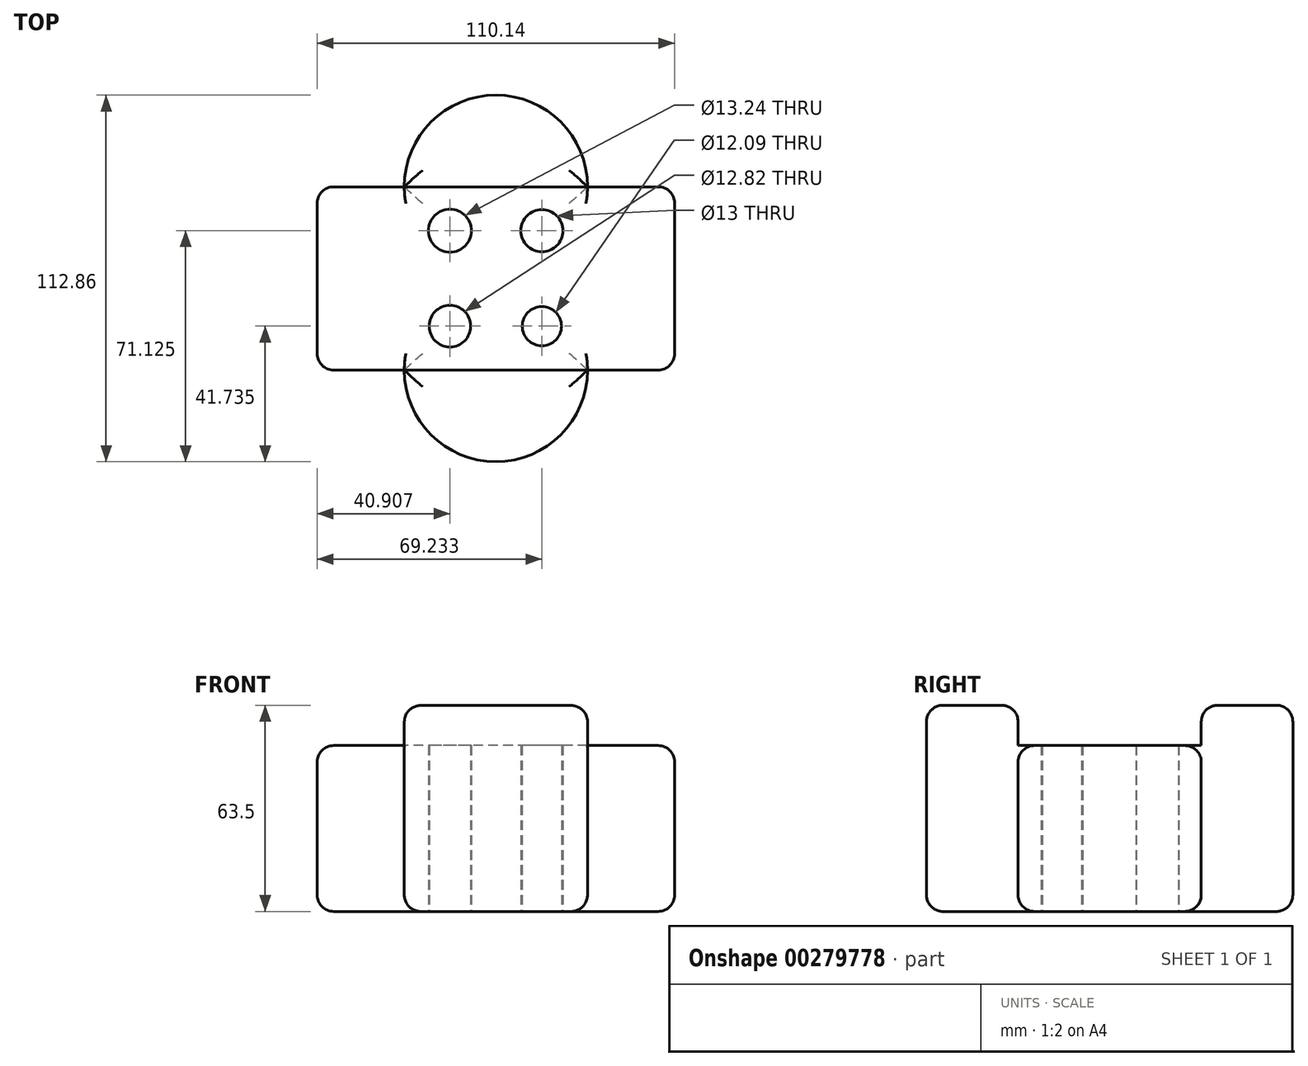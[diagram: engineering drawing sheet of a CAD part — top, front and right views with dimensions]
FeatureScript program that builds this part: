
annotation { "Feature Type Name" : "Feature", "Feature Type Description" : "" }
export const myFeature = defineFeature(function(context is Context, id is Id, definition is map)
    precondition{}
    {
        {
            var Q0;
            Q0=qCreatedBy(makeId("Top.planeOp"),FACE);
            var sketch = newSketch(context, id + "F0", { "sketchPlane" : qUnion([Q0])});
            skLineSegment(sketch, "E0.bottom", {"start": v(55.07, 28.22) * mm, "end": v(-55.07, 28.22) * mm});
            skLineSegment(sketch, "E0.top", {"start": v(55.07, -28.22) * mm, "end": v(-55.07, -28.22) * mm});
            skLineSegment(sketch, "E0.left", {"start": v(55.07, 28.22) * mm, "end": v(55.07, -28.22) * mm});
            skLineSegment(sketch, "E0.right", {"start": v(-55.07, 28.22) * mm, "end": v(-55.07, -28.22) * mm});
            skPoint(sketch, "E0.middle", {"position": v(0, 0) * mm});
            skCircle(sketch, "E1", {"center": v(0, 28.22) * mm, "radius": 28.22 * mm});
            skCircle(sketch, "E2", {"center": v(0, -28.22) * mm, "radius": 28.22 * mm});
            skLineSegment(sketch, "E3.bottom", {"start": v(14.16, 14.7) * mm, "end": v(-14.16, 14.7) * mm});
            skLineSegment(sketch, "E3.top", {"start": v(14.16, -14.7) * mm, "end": v(-14.16, -14.7) * mm});
            skLineSegment(sketch, "E3.left", {"start": v(14.16, 14.7) * mm, "end": v(14.16, -14.7) * mm});
            skLineSegment(sketch, "E3.right", {"start": v(-14.16, 14.7) * mm, "end": v(-14.16, -14.7) * mm});
            skCircle(sketch, "E4", {"center": v(14.16, 14.7) * mm, "radius": 6.5 * mm});
            skCircle(sketch, "E5", {"center": v(-14.16, 14.7) * mm, "radius": 6.62 * mm});
            skCircle(sketch, "E6", {"center": v(-14.16, -14.7) * mm, "radius": 6.4 * mm});
            skCircle(sketch, "E7", {"center": v(14.16, -14.7) * mm, "radius": 6.04 * mm});
            skSolve(sketch);
        }
        {
            var Q0;
            {var subQ5=sQuery(id+"F0.wireOp",EDGE,"E0.right");Q0=makeQuery(id+"F0.imprint","IMPRINT",FACE,{"disambiguationData":[TD([[makeQuery(id+"F0.imprint","IMPRINT",EDGE,{"derivedFrom":subQ5}),1.0]])]});}
            var Q1;
            {var subQ0=sQuery(id+"F0.wireOp",EDGE,"E2");var subQ1=sQuery(id+"F0.wireOp",EDGE,"E0.top");var subQ2=makeQuery(id+"F0.imprint","INTERSECT",VERTEX,{"disambiguationData":[OD(0.0)],"derivedFrom":[subQ1,subQ0]});Q1=makeQuery(id+"F0.imprint","IMPRINT",FACE,{"disambiguationData":[TD([[makeQuery(id+"F0.imprint","IMPRINT",EDGE,{"disambiguationData":[TD([[subQ2,-1.0]])],"derivedFrom":subQ1}),-1.0]])]});}
            var Q2;
            {var subQ0=sQuery(id+"F0.wireOp",EDGE,"E1");var subQ1=sQuery(id+"F0.wireOp",EDGE,"E0.bottom");var subQ2=makeQuery(id+"F0.imprint","INTERSECT",VERTEX,{"disambiguationData":[OD(0.0)],"derivedFrom":[subQ1,subQ0]});Q2=makeQuery(id+"F0.imprint","IMPRINT",FACE,{"disambiguationData":[TD([[makeQuery(id+"F0.imprint","IMPRINT",EDGE,{"disambiguationData":[TD([[subQ2,-1.0]])],"derivedFrom":subQ1}),1.0]])]});}
            var Q3;
            {var subQ0=sQuery(id+"F0.wireOp",EDGE,"E0.left");Q3=makeQuery(id+"F0.imprint","IMPRINT",FACE,{"disambiguationData":[TD([[makeQuery(id+"F0.imprint","IMPRINT",EDGE,{"derivedFrom":subQ0}),-1.0]])]});}
            var Q4;
            {var subQ0=sQuery(id+"F0.wireOp",EDGE,"E3.right");var subQ1=sQuery(id+"F0.wireOp",EDGE,"E1");var subQ2=makeQuery(id+"F0.imprint","INTERSECT",VERTEX,{"derivedFrom":[subQ1,subQ0]});Q4=makeQuery(id+"F0.imprint","IMPRINT",FACE,{"disambiguationData":[TD([[makeQuery(id+"F0.imprint","IMPRINT",EDGE,{"disambiguationData":[TD([[subQ2,-1.0]])],"derivedFrom":subQ1}),-1.0]])]});}
            var Q5;
            {var subQ0=sQuery(id+"F0.wireOp",EDGE,"E2");var subQ1=sQuery(id+"F0.wireOp",EDGE,"E1");var subQ2=makeQuery(id+"F0.imprint","INTERSECT",VERTEX,{"derivedFrom":[subQ1,subQ0]});Q5=makeQuery(id+"F0.imprint","IMPRINT",FACE,{"disambiguationData":[TD([[makeQuery(id+"F0.imprint","IMPRINT",EDGE,{"disambiguationData":[TD([[subQ2,-1.0]])],"derivedFrom":subQ1}),-1.0]])]});}
            var Q6;
            {var subQ5=sQuery(id+"F0.wireOp",EDGE,"E3.right");var subQ6=sQuery(id+"F0.wireOp",EDGE,"E1");var subQ7=makeQuery(id+"F0.imprint","INTERSECT",VERTEX,{"derivedFrom":[subQ6,subQ5]});Q6=makeQuery(id+"F0.imprint","IMPRINT",FACE,{"disambiguationData":[TD([[makeQuery(id+"F0.imprint","IMPRINT",EDGE,{"disambiguationData":[TD([[subQ7,-1.0]])],"derivedFrom":subQ6}),1.0]])]});}
            var Q7;
            {var subQ1=sQuery(id+"F0.wireOp",EDGE,"E2");var subQ11=makeQuery(id+"F0.imprint","INTERSECT",VERTEX,{"derivedFrom":[sQuery(id+"F0.wireOp",EDGE,"E1"),subQ1]});Q7=makeQuery(id+"F0.imprint","IMPRINT",FACE,{"disambiguationData":[TD([[makeQuery(id+"F0.imprint","IMPRINT",EDGE,{"disambiguationData":[TD([[subQ11,1.0]])],"derivedFrom":subQ1}),1.0]])]});}
            extrude(context, id + "F1", {"entities" : qUnion([Q0, Q1, Q2, Q3, Q4, Q5, Q6, Q7]), "depth" : 51.08 * mm});
        }
        {
            var Q0;
            {var subQ0=sQuery(id+"F0.wireOp",EDGE,"E1");var subQ1=sQuery(id+"F0.wireOp",EDGE,"E0.bottom");var subQ2=makeQuery(id+"F0.imprint","INTERSECT",VERTEX,{"disambiguationData":[OD(0.0)],"derivedFrom":[subQ1,subQ0]});Q0=makeQuery(id+"F0.imprint","IMPRINT",FACE,{"disambiguationData":[TD([[makeQuery(id+"F0.imprint","IMPRINT",EDGE,{"disambiguationData":[TD([[subQ2,-1.0]])],"derivedFrom":subQ1}),-1.0]])]});}
            var Q1;
            {var subQ0=sQuery(id+"F0.wireOp",EDGE,"E2");var subQ1=sQuery(id+"F0.wireOp",EDGE,"E0.top");var subQ2=makeQuery(id+"F0.imprint","INTERSECT",VERTEX,{"disambiguationData":[OD(0.0)],"derivedFrom":[subQ1,subQ0]});Q1=makeQuery(id+"F0.imprint","IMPRINT",FACE,{"disambiguationData":[TD([[makeQuery(id+"F0.imprint","IMPRINT",EDGE,{"disambiguationData":[TD([[subQ2,-1.0]])],"derivedFrom":subQ1}),1.0]])]});}
            extrude(context, id + "F2", {"entities" : qUnion([Q0, Q1]), "operationType" : NewBodyOperationType.ADD, "depth" : 63.5 * mm});
        }
        {
            var Q0;
            Q0=makeQuery(id+"F1.opExtrude","CAP_EDGE",EDGE,{"disambiguationData":[OSD([sQuery(id+"F0.wireOp",EDGE,"E0.right")])],"isStart":true});
            var Q1;
            {var subQ1=sQuery(id+"F0.wireOp",EDGE,"E0.bottom");var subQ2=sQuery(id+"F0.wireOp",EDGE,"E0.right");Q1=makeQuery(id+"F2.boolean.opBoolean","SPLIT",EDGE,{"disambiguationData":[TD([makeQuery(id+"F1.opExtrude","SWEPT_FACE",FACE,{"disambiguationData":[OSD([subQ2])]})])],"derivedFrom":makeQuery(id+"F1.opExtrude","CAP_EDGE",EDGE,{"disambiguationData":[OSD([subQ1])],"isStart":true})});}
            var Q2;
            Q2=makeQuery(id+"F2.opExtrude","CAP_EDGE",EDGE,{"disambiguationData":[OSD([sQuery(id+"F0.wireOp",EDGE,"E1")])],"isStart":true});
            var Q3;
            {var subQ1=sQuery(id+"F0.wireOp",EDGE,"E0.bottom");var subQ2=sQuery(id+"F0.wireOp",EDGE,"E0.left");Q3=makeQuery(id+"F2.boolean.opBoolean","SPLIT",EDGE,{"disambiguationData":[TD([makeQuery(id+"F1.opExtrude","SWEPT_FACE",FACE,{"disambiguationData":[OSD([subQ2])]})])],"derivedFrom":makeQuery(id+"F1.opExtrude","CAP_EDGE",EDGE,{"disambiguationData":[OSD([subQ1])],"isStart":true})});}
            var Q4;
            Q4=makeQuery(id+"F1.opExtrude","CAP_EDGE",EDGE,{"disambiguationData":[OSD([sQuery(id+"F0.wireOp",EDGE,"E0.left")])],"isStart":true});
            var Q5;
            {var subQ1=sQuery(id+"F0.wireOp",EDGE,"E0.left");var subQ2=sQuery(id+"F0.wireOp",EDGE,"E0.top");Q5=makeQuery(id+"F2.boolean.opBoolean","SPLIT",EDGE,{"disambiguationData":[TD([makeQuery(id+"F1.opExtrude","SWEPT_FACE",FACE,{"disambiguationData":[OSD([subQ1])]})])],"derivedFrom":makeQuery(id+"F1.opExtrude","CAP_EDGE",EDGE,{"disambiguationData":[OSD([subQ2])],"isStart":true})});}
            var Q6;
            Q6=makeQuery(id+"F2.opExtrude","CAP_EDGE",EDGE,{"disambiguationData":[OSD([sQuery(id+"F0.wireOp",EDGE,"E2")])],"isStart":true});
            var Q7;
            {var subQ1=sQuery(id+"F0.wireOp",EDGE,"E0.right");var subQ2=sQuery(id+"F0.wireOp",EDGE,"E0.top");Q7=makeQuery(id+"F2.boolean.opBoolean","SPLIT",EDGE,{"disambiguationData":[TD([makeQuery(id+"F1.opExtrude","SWEPT_FACE",FACE,{"disambiguationData":[OSD([subQ1])]})])],"derivedFrom":makeQuery(id+"F1.opExtrude","CAP_EDGE",EDGE,{"disambiguationData":[OSD([subQ2])],"isStart":true})});}
            var Q8;
            {var subQ0=sQuery(id+"F0.wireOp",EDGE,"E0.bottom");Q8=makeQuery(id+"F2.boolean.opBoolean","SPLIT",EDGE,{"disambiguationData":[topologyDisambiguationEdgeConnected([makeQuery(id+"F1.opExtrude","CAP_FACE",FACE,{"disambiguationData":[OSD([subQ0,sQuery(id+"F0.wireOp",EDGE,"E0.top"),sQuery(id+"F0.wireOp",EDGE,"E0.left"),sQuery(id+"F0.wireOp",EDGE,"E0.right")])],"isStart":false}),makeQuery(id+"F2.opExtrude","SWEPT_FACE",FACE,{"disambiguationData":[OSD([subQ0])]})])],"derivedFrom":makeQuery(id+"F1.opExtrude","CAP_EDGE",EDGE,{"disambiguationData":[OSD([subQ0])],"isStart":false})});}
            var Q9;
            Q9=makeQuery(id+"F2.opExtrude","CAP_EDGE",EDGE,{"disambiguationData":[OSD([sQuery(id+"F0.wireOp",EDGE,"E0.bottom")])],"isStart":false});
            var Q10;
            Q10=makeQuery(id+"F2.opExtrude","CAP_EDGE",EDGE,{"disambiguationData":[OSD([sQuery(id+"F0.wireOp",EDGE,"E0.top")])],"isStart":false});
            var Q11;
            {var subQ0=sQuery(id+"F0.wireOp",EDGE,"E0.top");Q11=makeQuery(id+"F2.boolean.opBoolean","SPLIT",EDGE,{"disambiguationData":[topologyDisambiguationEdgeConnected([makeQuery(id+"F1.opExtrude","CAP_FACE",FACE,{"disambiguationData":[OSD([sQuery(id+"F0.wireOp",EDGE,"E0.bottom"),subQ0,sQuery(id+"F0.wireOp",EDGE,"E0.left"),sQuery(id+"F0.wireOp",EDGE,"E0.right")])],"isStart":false}),makeQuery(id+"F2.opExtrude","SWEPT_FACE",FACE,{"disambiguationData":[OSD([subQ0])]})])],"derivedFrom":makeQuery(id+"F1.opExtrude","CAP_EDGE",EDGE,{"disambiguationData":[OSD([subQ0])],"isStart":false})});}
            var Q12;
            Q12=makeQuery(id+"F2.opExtrude","CAP_EDGE",EDGE,{"disambiguationData":[OSD([sQuery(id+"F0.wireOp",EDGE,"E2")])],"isStart":false});
            var Q13;
            Q13=makeQuery(id+"F2.opExtrude","CAP_EDGE",EDGE,{"disambiguationData":[OSD([sQuery(id+"F0.wireOp",EDGE,"E1")])],"isStart":false});
            var Q14;
            Q14=makeQuery(id+"F1.opExtrude","SWEPT_EDGE",EDGE,{"disambiguationData":[OSD([sQuery(id+"F0.wireOp",EDGE,"E0.top"),sQuery(id+"F0.wireOp",EDGE,"E0.right")])]});
            var Q15;
            Q15=makeQuery(id+"F1.opExtrude","SWEPT_EDGE",EDGE,{"disambiguationData":[OSD([sQuery(id+"F0.wireOp",EDGE,"E0.bottom"),sQuery(id+"F0.wireOp",EDGE,"E0.right")])]});
            var Q16;
            Q16=makeQuery(id+"F1.opExtrude","CAP_EDGE",EDGE,{"disambiguationData":[OSD([sQuery(id+"F0.wireOp",EDGE,"E0.right")])],"isStart":false});
            var Q17;
            Q17=makeQuery(id+"F1.opExtrude","SWEPT_EDGE",EDGE,{"disambiguationData":[OSD([sQuery(id+"F0.wireOp",EDGE,"E0.top"),sQuery(id+"F0.wireOp",EDGE,"E0.left")])]});
            var Q18;
            Q18=makeQuery(id+"F1.opExtrude","CAP_EDGE",EDGE,{"disambiguationData":[OSD([sQuery(id+"F0.wireOp",EDGE,"E0.left")])],"isStart":false});
            var Q19;
            Q19=makeQuery(id+"F1.opExtrude","SWEPT_EDGE",EDGE,{"disambiguationData":[OSD([sQuery(id+"F0.wireOp",EDGE,"E0.bottom"),sQuery(id+"F0.wireOp",EDGE,"E0.left")])]});
            fillet(context, id + "F3", {"entities" : qUnion([Q0, Q1, Q2, Q3, Q4, Q5, Q6, Q7, Q8, Q9, Q10, Q11, Q12, Q13, Q14, Q15, Q16, Q17, Q18, Q19]), "radius" : 5.08 * mm, "tangentPropagation" : true, "allowEdgeOverflow" : false});
        }
    });
